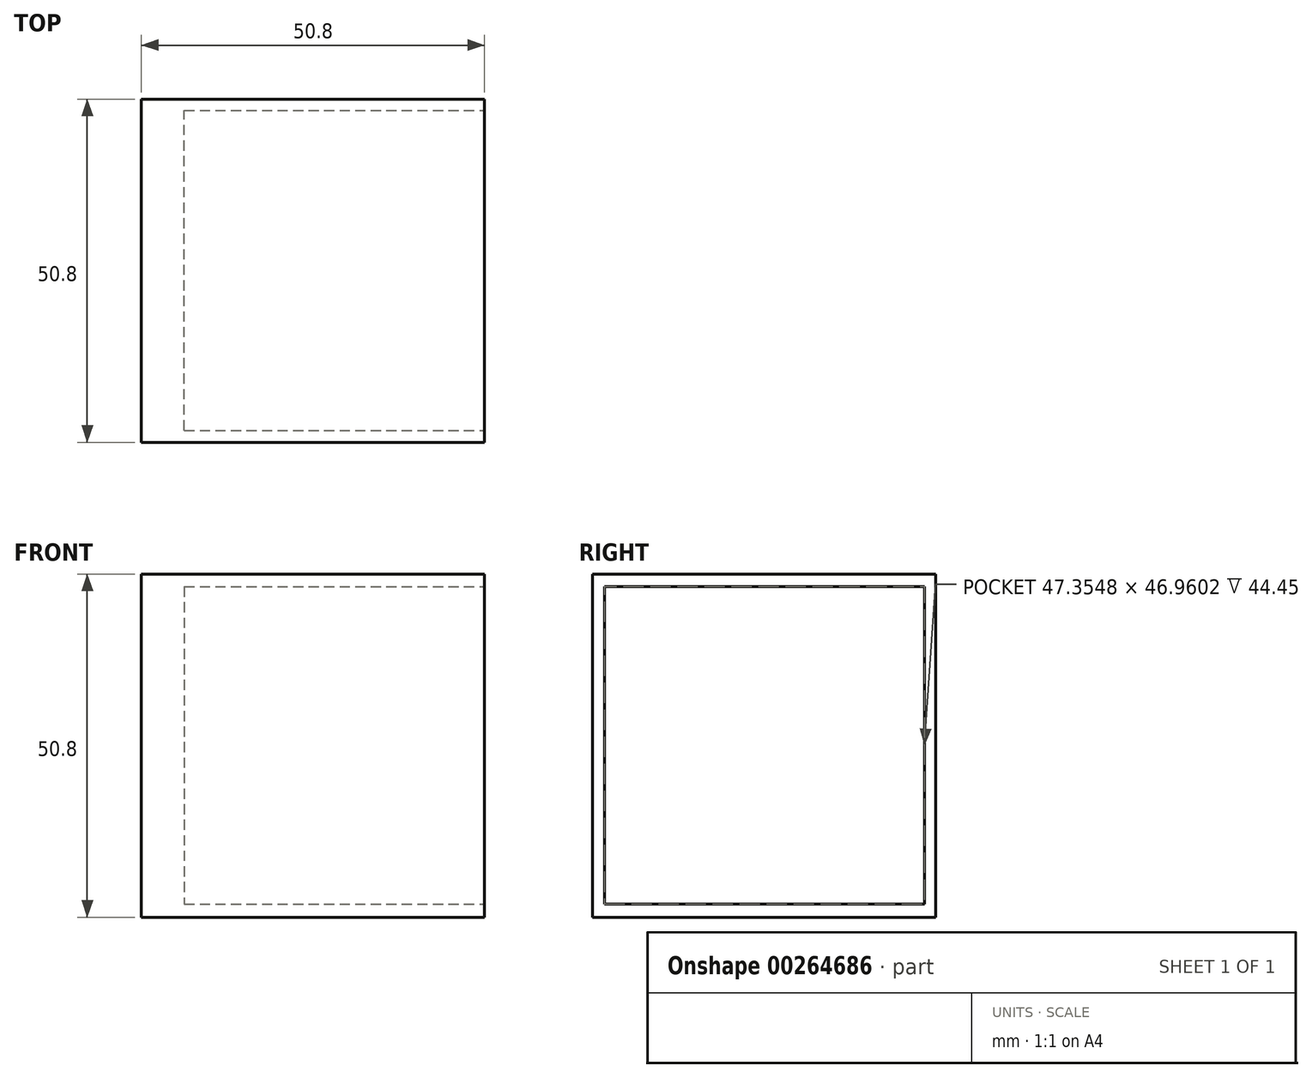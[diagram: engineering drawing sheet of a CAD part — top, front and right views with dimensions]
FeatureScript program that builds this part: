
annotation { "Feature Type Name" : "Feature", "Feature Type Description" : "" }
export const myFeature = defineFeature(function(context is Context, id is Id, definition is map)
    precondition{}
    {
        {
            var Q0;
            Q0=qCreatedBy(makeId("Front.planeOp"),FACE);
            var sketch = newSketch(context, id + "F0", { "sketchPlane" : qUnion([Q0])});
            skLineSegment(sketch, "E0.bottom", {"start": v(0, 0) * mm, "end": v(50.8, 0) * mm});
            skLineSegment(sketch, "E0.top", {"start": v(0, -50.8) * mm, "end": v(50.8, -50.8) * mm});
            skLineSegment(sketch, "E0.left", {"start": v(0, 0) * mm, "end": v(0, -50.8) * mm});
            skLineSegment(sketch, "E0.right", {"start": v(50.8, 0) * mm, "end": v(50.8, -50.8) * mm});
            skSolve(sketch);
        }
        {
            var Q0;
            Q0 = qSketchRegion(id + "F0", true);
            extrude(context, id + "F1", {"entities" : qUnion([Q0]), "depth" : 50.8 * mm});
        }
        {
            var Q0;
            Q0=qCreatedBy(makeId("Right.planeOp"),FACE);
            var sketch = newSketch(context, id + "F2", { "sketchPlane" : qUnion([Q0])});
            skLineSegment(sketch, "E1.bottom", {"start": v(-48.65, -2.07) * mm, "end": v(-2.27, -2.07) * mm});
            skLineSegment(sketch, "E1.top", {"start": v(-48.65, -48.83) * mm, "end": v(-2.27, -48.83) * mm});
            skLineSegment(sketch, "E1.left", {"start": v(-48.65, -2.07) * mm, "end": v(-48.65, -48.83) * mm});
            skLineSegment(sketch, "E1.right", {"start": v(-2.27, -2.07) * mm, "end": v(-2.27, -48.83) * mm});
            skSolve(sketch);
        }
        {
            var Q0;
            Q0 = qSketchRegion(id + "F2", true);
            extrude(context, id + "F3", {"entities" : qUnion([Q0]), "operationType" : NewBodyOperationType.REMOVE, "oppositeDirection" : true, "depth" : 44.45 * mm});
        }
        {
            var Q0;
            Q0=makeQuery(id+"F1.opExtrude","SWEPT_FACE",FACE,{"disambiguationData":[OSD([sQuery(id+"F0.wireOp",EDGE,"E0.right")])]});
            var sketch = newSketch(context, id + "F4", { "sketchPlane" : qUnion([Q0])});
            skLineSegment(sketch, "E2.bottom", {"start": v(-49.03, -1.87) * mm, "end": v(-1.68, -1.87) * mm});
            skLineSegment(sketch, "E2.top", {"start": v(-49.03, -48.83) * mm, "end": v(-1.68, -48.83) * mm});
            skLineSegment(sketch, "E2.left", {"start": v(-49.03, -1.87) * mm, "end": v(-49.03, -48.83) * mm});
            skLineSegment(sketch, "E2.right", {"start": v(-1.68, -1.87) * mm, "end": v(-1.68, -48.83) * mm});
            skSolve(sketch);
        }
        {
            var Q0;
            Q0=makeQuery(id+"F4.imprint","IMPRINT",FACE,{"disambiguationData":[TD([[makeQuery(id+"F4.imprint","IMPRINT",EDGE,{"derivedFrom":sQuery(id+"F4.wireOp",EDGE,"E2.bottom")}),-1.0]])]});
            extrude(context, id + "F5", {"entities" : qUnion([Q0]), "operationType" : NewBodyOperationType.REMOVE, "oppositeDirection" : true, "depth" : 44.45 * mm});
        }
    });
